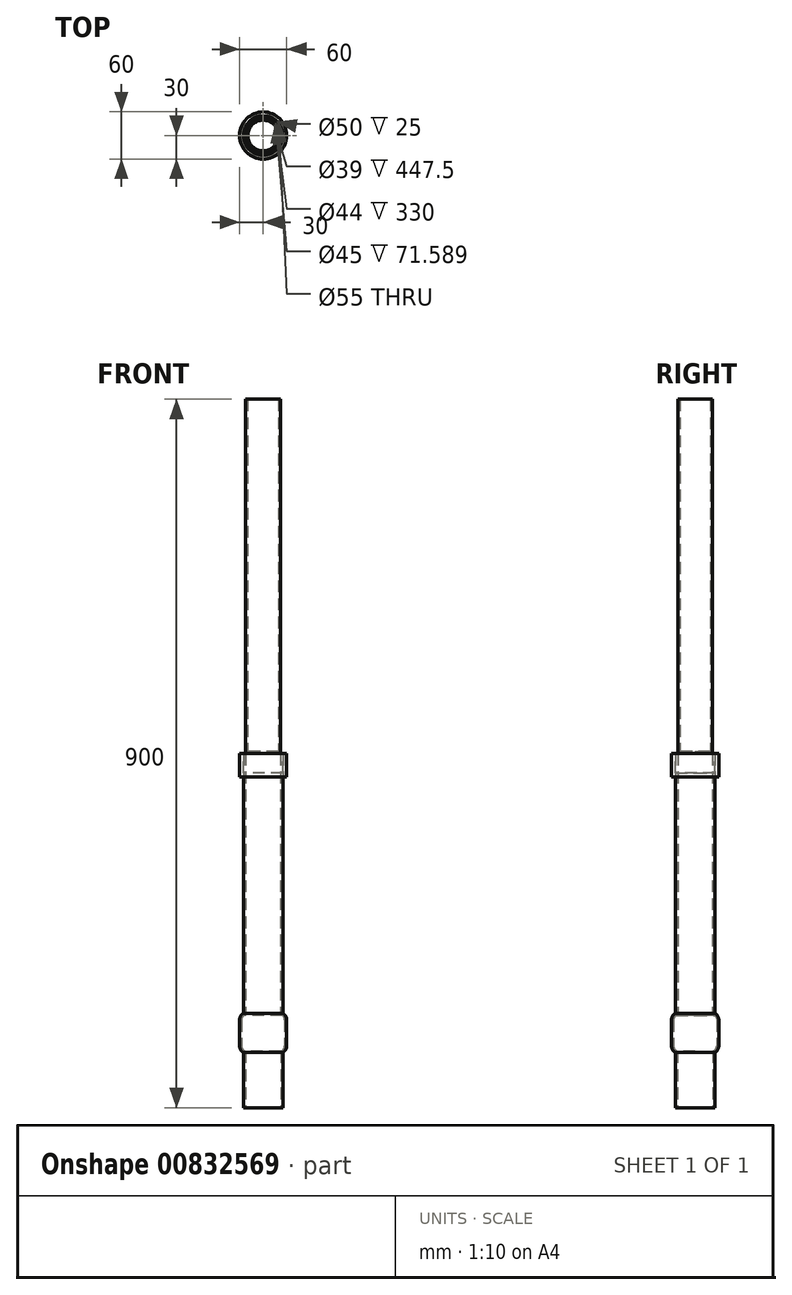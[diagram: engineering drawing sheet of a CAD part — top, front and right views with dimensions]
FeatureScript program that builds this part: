
annotation { "Feature Type Name" : "Feature", "Feature Type Description" : "" }
export const myFeature = defineFeature(function(context is Context, id is Id, definition is map)
    precondition{}
    {
        {
            var Q0;
            Q0=qCreatedBy(makeId("Top.planeOp"),FACE);
            var sketch = newSketch(context, id + "F0", { "sketchPlane" : qUnion([Q0])});
            skCircle(sketch, "E0", {"center": v(0, 0) * mm, "radius": 25 * mm});
            skSolve(sketch);
        }
        {
            var Q0;
            Q0=makeQuery(id+"F0.imprint","IMPRINT",FACE,{"disambiguationData":[TD([[makeQuery(id+"F0.imprint","IMPRINT",EDGE,{"derivedFrom":sQuery(id+"F0.wireOp",EDGE,"E0")}),1.0]])]});
            extrude(context, id + "F1", {"entities" : qUnion([Q0]), "depth" : 450 * mm, "offsetDistance" : 25 * mm});
        }
        {
            var Q0;
            Q0=makeQuery(id+"F1.opExtrude","CAP_FACE",FACE,{"disambiguationData":[OSD([sQuery(id+"F0.wireOp",EDGE,"E0")])],"isStart":false});
            shell(context, id + "F2", {"entities" : qUnion([Q0]), "thickness" : 3 * mm});
        }
        {
            var Q0;
            Q0=makeQuery(id+"F1.opExtrude","CAP_FACE",FACE,{"disambiguationData":[OSD([sQuery(id+"F0.wireOp",EDGE,"E0")])],"isStart":false});
            var sketch = newSketch(context, id + "F3", { "sketchPlane" : qUnion([Q0])});
            skSolve(sketch);
        }
        {
            var Q0;
            Q0 = qSketchRegion(id + "F3", true);
            var Q1;
            {var subQ0=sQuery(id+"F0.wireOp",EDGE,"E0");Q1=makeQuery(id+"F3.imprint","IMPRINT",FACE,{"disambiguationData":[TD([[makeQuery(id+"F3.imprint","IMPRINT",EDGE,{"derivedFrom":makeQuery(id+"F2.opShell","OFFSET_EDGE",EDGE,{"disambiguationData":[OSD([subQ0]),TDD([makeQuery(id+"F1.opExtrude","CAP_EDGE",EDGE,{"disambiguationData":[OSD([subQ0])],"isStart":false})])]})}),1.0]])]});}
            extrude(context, id + "F4", {"entities" : qUnion([Q0, Q1]), "depth" : 450 * mm, "offsetDistance" : 25 * mm});
        }
        {
            var Q0;
            Q0=makeQuery(id+"F4.opExtrude","CAP_FACE",FACE,{"disambiguationData":[OSD([sQuery(id+"F0.wireOp",EDGE,"E0")])],"isStart":false});
            shell(context, id + "F5", {"entities" : qUnion([Q0]), "thickness" : 2.5 * mm});
        }
        {
            var Q0;
            Q0=qCreatedBy(makeId("Top.planeOp"),FACE);
            cPlane(context, id + "F6", {"entities" : qUnion([Q0]), "cplaneType" : CPlaneType.OFFSET, "offset" : 70 * mm, "width" : 150 * mm, "height" : 150 * mm});
        }
        {
            var Q0;
            Q0=qCreatedBy(id+"F6.planeOp",FACE);
            var sketch = newSketch(context, id + "F7", { "sketchPlane" : qUnion([Q0])});
            skCircle(sketch, "E1", {"center": v(0, 0) * mm, "radius": 30 * mm});
            skSolve(sketch);
        }
        {
            var Q0;
            Q0=makeQuery(id+"F7.imprint","IMPRINT",FACE,{"disambiguationData":[TD([[makeQuery(id+"F7.imprint","IMPRINT",EDGE,{"derivedFrom":sQuery(id+"F7.wireOp",EDGE,"E1")}),1.0]])]});
            extrude(context, id + "F8", {"entities" : qUnion([Q0]), "operationType" : NewBodyOperationType.ADD, "depth" : 50 * mm, "offsetDistance" : 25 * mm});
        }
        {
            var Q0;
            Q0=makeQuery(id+"F8.opExtrude","CAP_EDGE",EDGE,{"disambiguationData":[OSD([sQuery(id+"F7.wireOp",EDGE,"E1")])],"isStart":false});
            var Q1;
            Q1=makeQuery(id+"F8.opExtrude","CAP_EDGE",EDGE,{"disambiguationData":[OSD([sQuery(id+"F7.wireOp",EDGE,"E1")])],"isStart":true});
            fillet(context, id + "F9", {"entities" : qUnion([Q0, Q1]), "radius" : 10 * mm, "tangentPropagation" : true, "allowEdgeOverflow" : false});
        }
        {
            var Q0;
            Q0=qCreatedBy(makeId("Top.planeOp"),FACE);
            cPlane(context, id + "F10", {"entities" : qUnion([Q0]), "cplaneType" : CPlaneType.OFFSET, "offset" : 450 * mm, "width" : 150 * mm, "height" : 150 * mm});
        }
        {
            var Q0;
            Q0=qCreatedBy(id+"F10.planeOp",FACE);
            var sketch = newSketch(context, id + "F11", { "sketchPlane" : qUnion([Q0])});
            skCircle(sketch, "E2", {"center": v(0, 0) * mm, "radius": 30 * mm});
            skSolve(sketch);
        }
        {
            var Q0;
            Q0=makeQuery(id+"F11.imprint","IMPRINT",FACE,{"disambiguationData":[TD([[makeQuery(id+"F11.imprint","IMPRINT",EDGE,{"derivedFrom":sQuery(id+"F11.wireOp",EDGE,"E2")}),1.0]])]});
            extrude(context, id + "F12", {"entities" : qUnion([Q0]), "oppositeDirection" : true, "depth" : 30 * mm, "offsetDistance" : 25 * mm});
        }
        {
            var Q0;
            Q0=makeQuery(id+"F12.opExtrude","CAP_FACE",FACE,{"disambiguationData":[OSD([sQuery(id+"F11.wireOp",EDGE,"E2")])],"isStart":true});
            shell(context, id + "F13", {"entities" : qUnion([Q0]), "thickness" : 5 * mm});
        }
        {
            var Q0;
            Q0=makeQuery(id+"F1.opExtrude","CAP_FACE",FACE,{"disambiguationData":[OSD([sQuery(id+"F0.wireOp",EDGE,"E0")])],"isStart":true});
            shell(context, id + "F14", {"entities" : qUnion([Q0]), "thickness" : 2.5 * mm});
        }
    });
